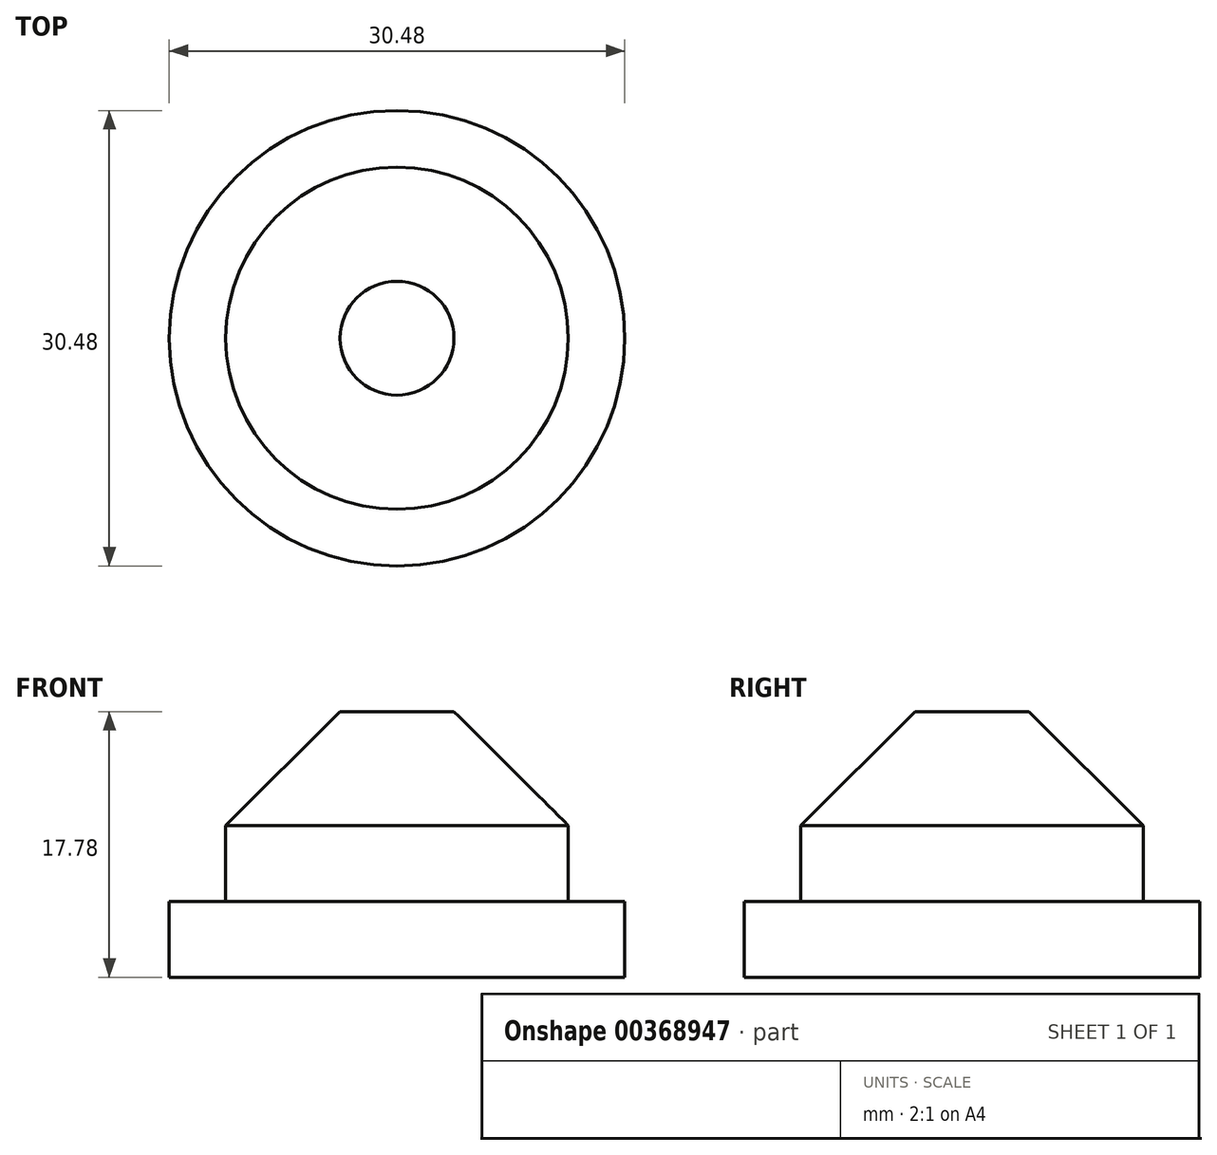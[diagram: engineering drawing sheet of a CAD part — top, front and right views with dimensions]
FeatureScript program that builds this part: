
annotation { "Feature Type Name" : "Feature", "Feature Type Description" : "" }
export const myFeature = defineFeature(function(context is Context, id is Id, definition is map)
    precondition{}
    {
        {
            var Q0;
            Q0=qCreatedBy(makeId("Top.planeOp"),FACE);
            var sketch = newSketch(context, id + "F0", { "sketchPlane" : qUnion([Q0])});
            skCircle(sketch, "E0", {"center": v(0, 0) * mm, "radius": 12.7 * mm});
            skSolve(sketch);
        }
        {
            var Q0;
            Q0 = qSketchRegion(id + "F0", true);
            extrude(context, id + "F1", {"entities" : qUnion([Q0]), "depth" : 7.62 * mm});
        }
        {
            var Q0;
            Q0=makeQuery(id+"F1.opExtrude","CAP_EDGE",EDGE,{"disambiguationData":[OSD([sQuery(id+"F0.wireOp",EDGE,"E0")])],"isStart":false});
            chamfer(context, id + "F2", {"entities" : qUnion([Q0]), "chamferType" : ChamferType.OFFSET_ANGLE, "width" : 8.9 * mm, "oppositeDirection" : false, "angle" : 44.9 * degree, "tangentPropagation" : true});
        }
        {
            var Q0;
            Q0=makeQuery(id+"F1.opExtrude","CAP_FACE",FACE,{"disambiguationData":[OSD([sQuery(id+"F0.wireOp",EDGE,"E0")])],"isStart":true});
            extrude(context, id + "F3", {"entities" : qUnion([Q0]), "operationType" : NewBodyOperationType.ADD, "depth" : 5.08 * mm});
        }
        {
            var Q0;
            Q0=makeQuery(id+"F3.opExtrude","CAP_FACE",FACE,{"disambiguationData":[OSD([sQuery(id+"F0.wireOp",EDGE,"E0")])],"isStart":false});
            var sketch = newSketch(context, id + "F4", { "sketchPlane" : qUnion([Q0])});
            skCircle(sketch, "E1", {"center": v(0, 0) * mm, "radius": 15.24 * mm});
            skSolve(sketch);
        }
        {
            var Q0;
            Q0=makeQuery(id+"F4.imprint","IMPRINT",FACE,{"disambiguationData":[TD([[makeQuery(id+"F4.imprint","IMPRINT",EDGE,{"derivedFrom":makeQuery(id+"F3.opExtrude","CAP_EDGE",EDGE,{"disambiguationData":[OSD([sQuery(id+"F0.wireOp",EDGE,"E0")])],"isStart":false})}),1.0]])]});
            var sketch = newSketch(context, id + "F5", { "sketchPlane" : qUnion([Q0])});
            skCircle(sketch, "E2", {"center": v(0, 0) * mm, "radius": 13.97 * mm});
            skSolve(sketch);
        }
        {
            var Q0;
            Q0=sQuery(id+"F4.wireOp",EDGE,"E1");
            extrude(context, id + "F6", {"bodyType" : ToolBodyType.SURFACE, "surfaceEntities" : qUnion([Q0]), "oppositeDirection" : true, "depth" : 25.4 * mm});
        }
        {
            var Q0;
            Q0=makeQuery(id+"F5.imprint","IMPRINT",FACE,{"disambiguationData":[TD([[makeQuery(id+"F5.imprint","IMPRINT",EDGE,{"derivedFrom":makeQuery(id+"F4.imprint","IMPRINT",EDGE,{"derivedFrom":makeQuery(id+"F3.opExtrude","CAP_EDGE",EDGE,{"disambiguationData":[OSD([sQuery(id+"F0.wireOp",EDGE,"E0")])],"isStart":false})})}),1.0]])]});
            var sketch = newSketch(context, id + "F7", { "sketchPlane" : qUnion([Q0])});
            skCircle(sketch, "E3", {"center": v(0, 0) * mm, "radius": 15.24 * mm});
            skSolve(sketch);
        }
        {
            var Q0;
            Q0 = qSketchRegion(id + "F7", true);
            extrude(context, id + "F8", {"entities" : qUnion([Q0]), "operationType" : NewBodyOperationType.ADD, "depth" : 5.08 * mm});
        }
    });
